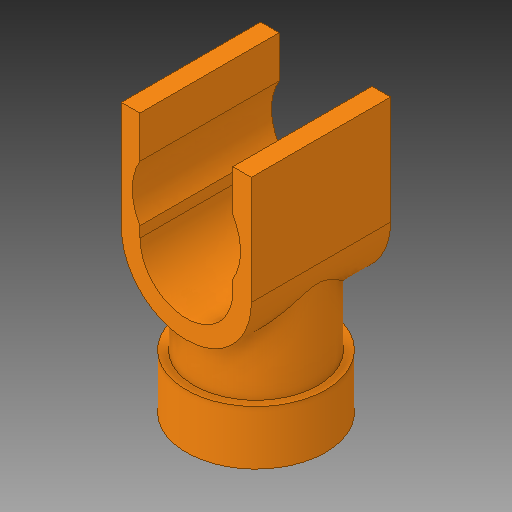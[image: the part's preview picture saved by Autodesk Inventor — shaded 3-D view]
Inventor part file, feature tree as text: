
AUTODESK INVENTOR PART (.ipt)
format: ipt  version: 2018 (Build 220112000, 112)  size: 199,168 bytes
history: native  units: mm
features: extrude x6, sketch x5, fillet x2
ambient origin geometry x8: Origin, YZ Plane, XZ Plane, XY Plane, X Axis, Y Axis, Z Axis, Center Point
bodies: Solid1 (feature_tree)
feature tree (13):
  extrude  "Extrusion1"  Depth=9.0mm
  extrude  "Extrusion5"  Depth=3.5mm
  extrude  "Extrusion6"  Depth=7.3mm
  extrude  "Extrusion2"  Depth=8.0mm TaperAngle=0.0deg
  sketch  "Sketch3"  dims[d7=18.0mm d8=0.0mm d9=7.3mm]
  extrude  "Extrusion3"  Depth=1.0mm
  extrude  "Extrusion4"  Depth=1.0mm
  fillet  "Fillet1"  Radius=0.26mm
  fillet  "Fillet2"  Radius=0.7mm
  sketch  "Sketch1"  dims[d1=2.23mm d3=9.0mm]
  sketch  "Sketch2"  dims[d4=3.5mm d5=0.0mm d6=2.0mm]
  sketch  "Sketch4"  dims[d10=2.0mm d11=8.0mm d12=0.0mm]
  sketch  "Sketch8"  dims[d13=12.0mm d14=0.0mm d15=1.0mm d16=1.0mm d18=0.26mm d19=0.7mm d20=3.75mm d21=3.0mm d23=1.2mm d24=7.0mm d25=7.0mm d26=7.0mm d27=2.5mm d28=9.0mm d29=0.0mm d33=8.0mm d34=9.0mm d35=0.0mm]
